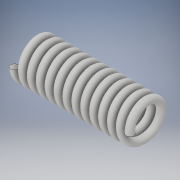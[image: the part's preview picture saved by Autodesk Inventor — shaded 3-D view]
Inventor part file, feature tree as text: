
AUTODESK INVENTOR PART (.ipt)
format: ipt  version: 2018.3 (Build 223284000, 284)  size: 459,264 bytes
history: native  units: in
note: dims shown in document units (in); Inventor stores cm internally (conversion verified against a paired STEP export)
features: helix x1, sketch x1
ambient origin geometry x8: Origin, YZ Plane, XZ Plane, XY Plane, X Axis, Y Axis, Z Axis, Center Point
bodies: Solid1 (feature_tree)
feature tree (2):
  helix  "Coil1"  [1 undecoded]
  sketch  "Sketch1"  dims[d1=0.593in d2=0.279in d3=5.1181in d4=0.0in d5=90.0deg d6=90.0deg d7=0.0in d8=0.0in d9=0.104in d10=0.279in]
note: 1 required parameter value undecoded (feature->parameter linkage not recoverable at this tier; creation-order binding heuristic only, values carry confidence <= 0.55)
